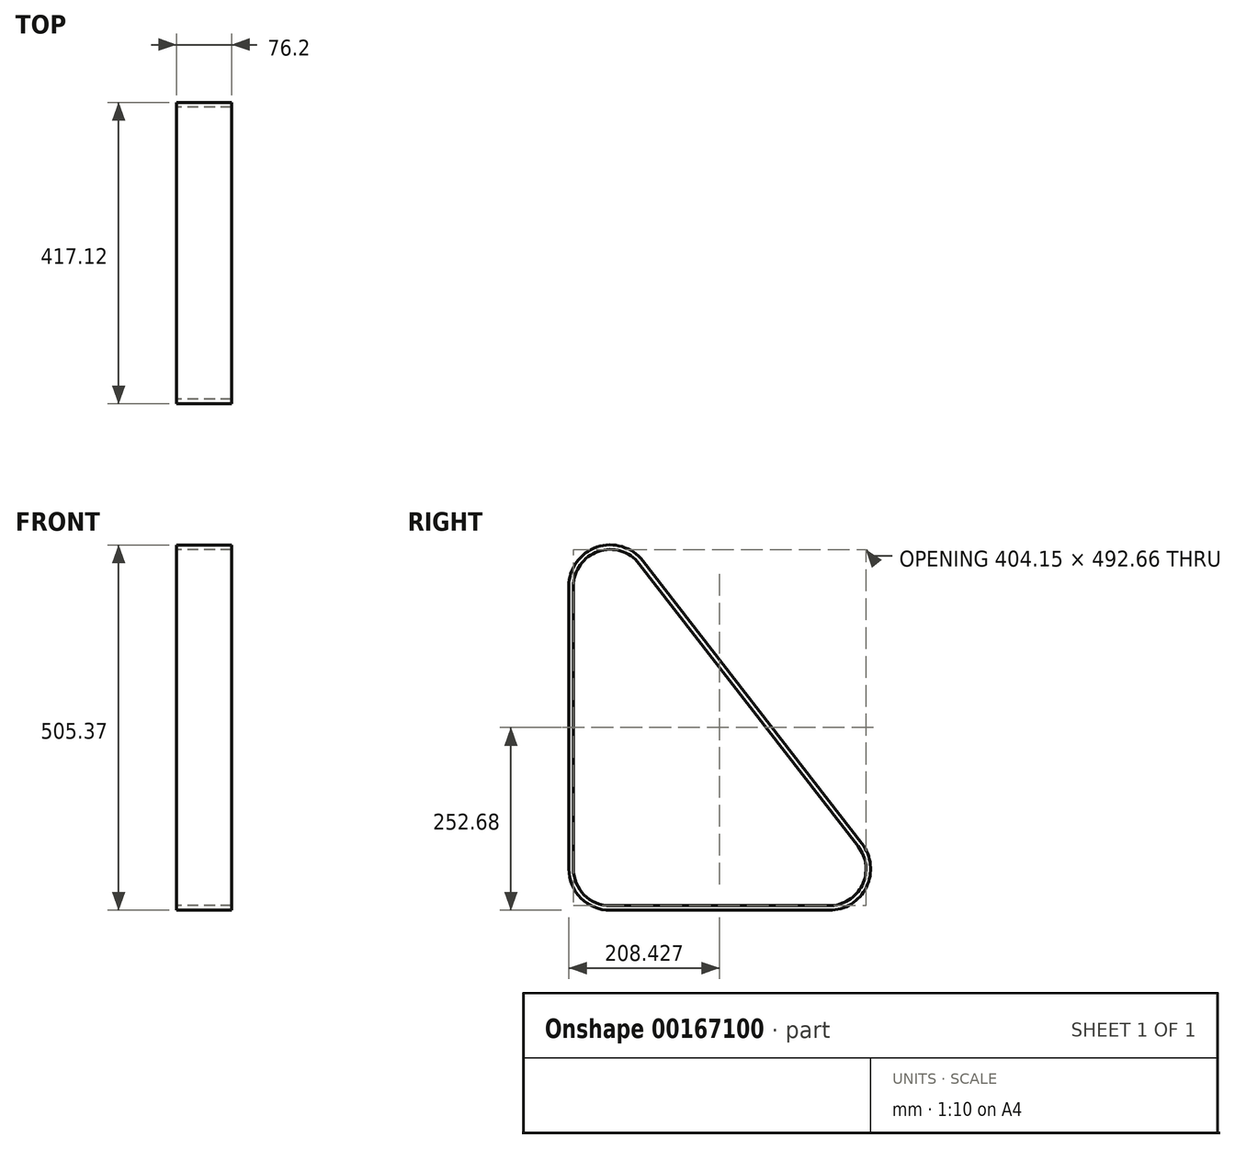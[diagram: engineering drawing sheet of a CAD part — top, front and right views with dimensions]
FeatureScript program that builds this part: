
annotation { "Feature Type Name" : "Feature", "Feature Type Description" : "" }
export const myFeature = defineFeature(function(context is Context, id is Id, definition is map)
    precondition{}
    {
        {
            var Q0;
            Q0=qCreatedBy(makeId("Right.planeOp"),FACE);
            var sketch = newSketch(context, id + "F0", { "sketchPlane" : qUnion([Q0])});
            skLineSegment(sketch, "E0", {"start": v(0, 441.87) * mm, "end": v(0, 50.8) * mm});
            skLineSegment(sketch, "E1", {"start": v(50.8, 0) * mm, "end": v(353.62, 0) * mm});
            skLineSegment(sketch, "E2", {"start": v(393.78, 81.9) * mm, "end": v(90.97, 472.97) * mm});
            skPoint(sketch, "E3.visualSharp", {"position": v(0, 590.45) * mm});
            skArc(sketch, "E3.filletArc", {"start": v(90.97, 472.97) * mm, "mid": v(34.37, 489.94) * mm, "end": v(0, 441.87) * mm});
            skPoint(sketch, "E4.visualSharp", {"position": v(0, 0) * mm});
            skArc(sketch, "E4.filletArc", {"start": v(0, 50.8) * mm, "mid": v(14.88, 14.88) * mm, "end": v(50.8, 0) * mm});
            skPoint(sketch, "E5.visualSharp", {"position": v(457.2, 0) * mm});
            skArc(sketch, "E5.filletArc", {"start": v(353.62, 0) * mm, "mid": v(399.23, 28.43) * mm, "end": v(393.78, 81.9) * mm});
            skLineSegment(sketch, "E6.0", {"start": v(50.8, -6.35) * mm, "end": v(353.62, -6.35) * mm});
            skLineSegment(sketch, "E6.1", {"start": v(398.8, 85.79) * mm, "end": v(95.99, 476.86) * mm});
            skArc(sketch, "E6.2", {"start": v(95.99, 476.86) * mm, "mid": v(32.31, 495.95) * mm, "end": v(-6.35, 441.87) * mm});
            skArc(sketch, "E6.3", {"start": v(353.62, -6.35) * mm, "mid": v(404.93, 25.64) * mm, "end": v(398.8, 85.79) * mm});
            skLineSegment(sketch, "E6.4", {"start": v(-6.35, 441.87) * mm, "end": v(-6.35, 50.8) * mm});
            skArc(sketch, "E6.5", {"start": v(-6.35, 50.8) * mm, "mid": v(10.39, 10.39) * mm, "end": v(50.8, -6.35) * mm});
            skSolve(sketch);
        }
        {
            var Q0;
            Q0=makeQuery(id+"F0.imprint","IMPRINT",FACE,{"disambiguationData":[TD([[makeQuery(id+"F0.imprint","IMPRINT",EDGE,{"derivedFrom":sQuery(id+"F0.wireOp",EDGE,"E0")}),-1.0]])]});
            extrude(context, id + "F1", {"entities" : qUnion([Q0]), "endBound" : BoundingType.SYMMETRIC, "depth" : 76.2 * mm});
        }
    });
